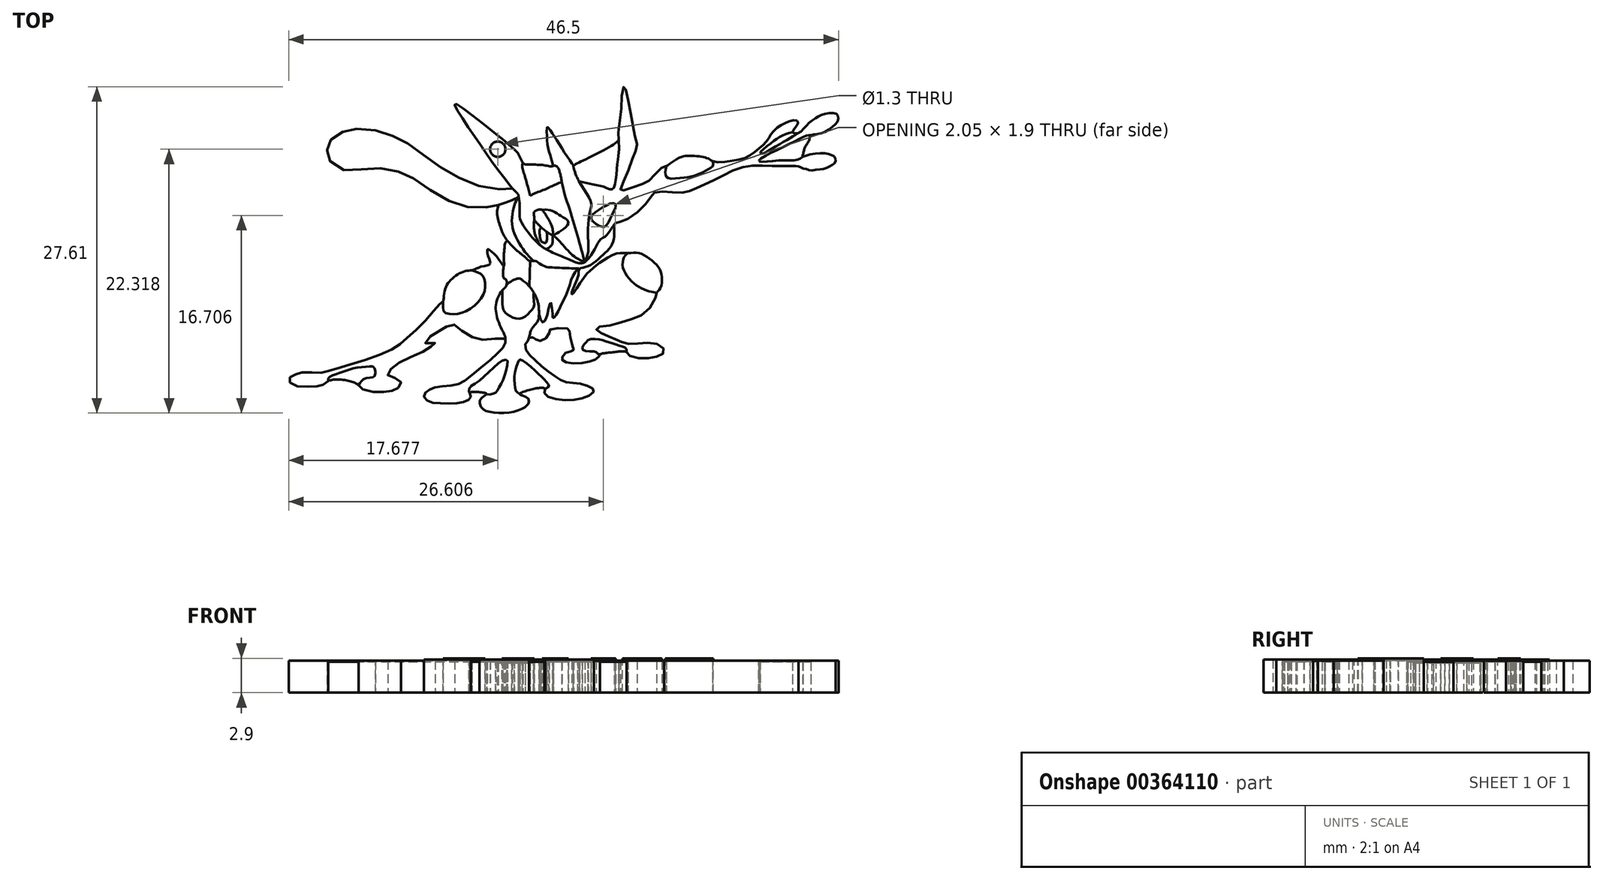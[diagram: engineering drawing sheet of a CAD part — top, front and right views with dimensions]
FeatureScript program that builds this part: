
annotation { "Feature Type Name" : "Feature", "Feature Type Description" : "" }
export const myFeature = defineFeature(function(context is Context, id is Id, definition is map)
    precondition{}
    {
        {
            var Q0;
            Q0=qCreatedBy(makeId("Top.planeOp"),FACE);
            var sketch = newSketch(context, id + "F0", { "sketchPlane" : qUnion([Q0])});
            skFitSpline(sketch, "E0", {"points": [v(20.96, 7.13) * mm, v(21.17, 7.03) * mm, v(21.4, 6.93) * mm, v(21.64, 6.89) * mm, v(21.9, 6.8) * mm, v(22.24, 6.8) * mm, v(22.73, 6.85) * mm, v(23.11, 6.9) * mm, v(23.47, 7.05) * mm, v(23.75, 7.22) * mm, v(23.95, 7.33) * mm, v(24.1, 7.54) * mm, v(24.1, 7.71) * mm, v(24.03, 7.9) * mm, v(23.83, 8.05) * mm, v(23.6, 8.14) * mm, v(23.11, 8.23) * mm, v(22.42, 8.19) * mm, v(21.64, 8.04) * mm, v(21.32, 7.94) * mm, v(21.38, 8.3) * mm, v(21.53, 8.8) * mm, v(21.85, 9.33) * mm, v(22, 9.74) * mm, v(22.47, 9.84) * mm, v(23.3, 10.1) * mm, v(23.97, 10.6) * mm, v(24.32, 11.05) * mm, v(24.27, 11.46) * mm, v(23.96, 11.64) * mm, v(23.1, 11.54) * mm, v(22.55, 11.31) * mm, v(21.95, 10.88) * mm, v(21.44, 10.36) * mm, v(20.9, 9.92) * mm, v(20.44, 10.02) * mm, v(20.63, 10.34) * mm, v(20.9, 10.7) * mm, v(20.9, 10.94) * mm, v(20.66, 11.03) * mm, v(20.12, 10.9) * mm, v(19.6, 10.66) * mm, v(19.05, 10.31) * mm, v(18.63, 9.82) * mm, v(18.36, 9.38) * mm, v(18.02, 8.98) * mm, v(17.3, 8.38) * mm, v(16.47, 7.85) * mm, v(15.29, 7.6) * mm, v(13.88, 7.5) * mm, v(13.36, 7.76) * mm, v(12.7, 7.94) * mm, v(11.76, 8.01) * mm, v(10.8, 7.82) * mm, v(9.8, 7.15) * mm, v(9.6, 7.1) * mm, v(9.06, 6.71) * mm, v(8.45, 6) * mm, v(8.02, 5.76) * mm, v(7.14, 5.4) * mm, v(6.2, 5.1) * mm, v(6.01, 5.05) * mm, v(5.9, 5.17) * mm, v(6.2, 5.92) * mm, v(6.75, 7.35) * mm, v(7.13, 8.3) * mm, v(7.3, 8.8) * mm, v(7.2, 9.4) * mm, v(6.99, 10.4) * mm, v(6.66, 12.13) * mm, v(6.36, 13.55) * mm, v(6.29, 13.84) * mm, v(6.13, 13.8) * mm, v(6, 12.67) * mm, v(5.87, 11.09) * mm, v(5.72, 9.72) * mm, v(5.66, 9.24) * mm, v(2.03, 7.26) * mm, v(1.91, 7.22) * mm, v(1.24, 8.18) * mm, v(0.3, 9.68) * mm, v(-0.21, 10.4) * mm, v(-0.3, 10.44) * mm, v(-0.3, 9.4) * mm, v(-0.1, 8.22) * mm, v(0.15, 7.15) * mm, v(-0.26, 7.17) * mm, v(-1.67, 7.27) * mm, v(-2.36, 7.39) * mm, v(-2.7, 8.13) * mm, v(-3.18, 8.63) * mm, v(-4.36, 9.64) * mm, v(-5.7, 10.68) * mm, v(-7.95, 12.37) * mm, v(-8.14, 12.37) * mm, v(-7.61, 11.39) * mm, v(-6.06, 9.1) * mm, v(-4.7, 7.13) * mm, v(-3.3, 5.33) * mm, v(-3.24, 5.24) * mm, v(-3.8, 5.19) * mm, v(-5.83, 5.38) * mm, v(-8, 6.3) * mm, v(-9.97, 7.48) * mm, v(-11.69, 8.77) * mm, v(-13, 9.52) * mm, v(-14.42, 10.09) * mm, v(-16.33, 10.3) * mm, v(-17.38, 10.13) * mm, v(-18.36, 9.55) * mm, v(-18.81, 9.06) * mm, v(-18.92, 8.39) * mm, v(-18.82, 7.81) * mm, v(-17.88, 6.93) * mm, v(-16.49, 6.8) * mm, v(-14.6, 6.95) * mm, v(-12.94, 6.7) * mm, v(-11.62, 6.1) * mm, v(-9.83, 4.86) * mm, v(-7.8, 3.86) * mm, v(-6.1, 3.63) * mm, v(-4.58, 3.8) * mm, v(-4.43, 3.84) * mm, v(-4.53, 3.33) * mm, v(-4.31, 2.17) * mm, v(-3.93, 1.22) * mm, v(-3.12, 0.24) * mm, v(-2.16, -0.56) * mm], "startDerivative": vector(49.3, -24.54) * mm, "endDerivative": vector(100.47, -77.23) * mm});
            skFitSpline(sketch, "E1", {"points": [v(-3.67, 0.84) * mm, v(-3.85, 0.65) * mm, v(-3.92, 0.1) * mm, v(-3.97, -0.66) * mm, v(-3.97, -1.29) * mm, v(-4.6, -0.48) * mm, v(-5.3, 0.11) * mm, v(-5.35, 0.1) * mm, v(-5.31, -0.46) * mm, v(-5.13, -1.13) * mm, v(-5.89, -1.36) * mm, v(-6.55, -1.64) * mm, v(-7.32, -1.76) * mm, v(-8.32, -2.35) * mm, v(-8.94, -3.3) * mm, v(-9.15, -4.35) * mm, v(-9.35, -4.48) * mm, v(-10.43, -5.76) * mm, v(-12.26, -7.47) * mm, v(-13.42, -8.36) * mm, v(-16.63, -9.53) * mm, v(-18.93, -10.23) * mm, v(-19.51, -10.34) * mm, v(-21.08, -10.32) * mm, v(-21.64, -10.5) * mm, v(-22.15, -10.87) * mm, v(-21.79, -11.37) * mm, v(-20.2, -11.52) * mm, v(-19.39, -11.4) * mm, v(-18.81, -11.03) * mm, v(-17.28, -10.99) * mm, v(-16.28, -11.38) * mm, v(-16.05, -11.67) * mm, v(-14.83, -11.97) * mm, v(-13.72, -11.92) * mm, v(-13.05, -11.72) * mm, v(-12.7, -11.37) * mm, v(-12.8, -10.92) * mm, v(-13.73, -10.63) * mm, v(-13.7, -10.26) * mm, v(-12.9, -9.53) * mm, v(-11, -8.65) * mm, v(-9.97, -8.03) * mm, v(-9.78, -7.83) * mm, v(-10.69, -7.78) * mm, v(-8.46, -6.27) * mm, v(-8.1, -6.32) * mm, v(-6.8, -7.25) * mm, v(-5.38, -7.54) * mm, v(-3.84, -7.45) * mm, v(-3.89, -7.94) * mm, v(-4.56, -8.74) * mm, v(-6.86, -10.7) * mm, v(-8.05, -11.36) * mm, v(-9.67, -11.56) * mm, v(-10.37, -11.84) * mm, v(-10.73, -12.23) * mm, v(-10.47, -12.69) * mm, v(-9.46, -12.92) * mm, v(-7.88, -12.92) * mm, v(-7.04, -12.68) * mm, v(-6.77, -12.39) * mm, v(-6.86, -12.05) * mm, v(-5.87, -12) * mm, v(-5.42, -12.14) * mm, v(-5.95, -12.56) * mm, v(-5.82, -13.33) * mm, v(-5, -13.68) * mm, v(-3.32, -13.68) * mm, v(-2.2, -13.25) * mm, v(-1.9, -12.95) * mm, v(-1.92, -12.51) * mm, v(-2.62, -12.14) * mm, v(-1.7, -11.77) * mm, v(-0.8, -11.61) * mm, v(-0.48, -11.71) * mm, v(-0.53, -12.03) * mm, v(-0.09, -12.44) * mm, v(1.43, -12.65) * mm, v(2.77, -12.46) * mm, v(3.56, -12.04) * mm, v(3.63, -11.78) * mm, v(3.22, -11.5) * mm, v(2.16, -11.22) * mm, v(1.26, -11.14) * mm, v(0.55, -10.75) * mm, v(-0.38, -10.11) * mm, v(-1.5, -9.1) * mm, v(-2.06, -8.45) * mm, v(-2.12, -7.85) * mm, v(-1.9, -7.6) * mm, v(-1.83, -7.35) * mm, v(-1.48, -7.38) * mm, v(-1.26, -7.53) * mm, v(-0.77, -7.64) * mm, v(-0.13, -6.97) * mm, v(-0.1, -6.71) * mm, v(1.46, -6.6) * mm, v(1.6, -6.89) * mm, v(1.84, -8.02) * mm, v(1.9, -8.47) * mm, v(1.36, -8.58) * mm, v(0.98, -9) * mm, v(0.98, -9.26) * mm, v(1.37, -9.48) * mm, v(2.9, -9.48) * mm, v(3.77, -9.2) * mm, v(4.08, -8.97) * mm, v(4.16, -8.8) * mm, v(5.06, -8.63) * mm, v(6.4, -8.59) * mm, v(6.64, -8.87) * mm, v(7.72, -9.12) * mm, v(8.8, -9.03) * mm, v(9.46, -8.75) * mm, v(9.57, -8.36) * mm, v(8.97, -7.9) * mm, v(7.67, -7.85) * mm, v(6.53, -7.9) * mm, v(5.82, -7.68) * mm, v(5.25, -7.43) * mm, v(4.38, -7.02) * mm, v(3.91, -6.74) * mm, v(3.88, -6.53) * mm, v(4.84, -6.36) * mm, v(6.58, -5.86) * mm, v(8.03, -5.24) * mm, v(8.91, -3.83) * mm, v(8.95, -3.57) * mm, v(9.28, -3.16) * mm, v(9.4, -2.31) * mm, v(9.17, -1.5) * mm, v(8.38, -0.7) * mm, v(7.47, -0.21) * mm, v(6.53, -0.22) * mm, v(5.66, -0.23) * mm, v(4.47, -0.8) * mm, v(3.57, -1.48) * mm, v(2.7, -2.42) * mm, v(1.8, -3.7) * mm, v(1.83, -3.4) * mm, v(2.32, -2.14) * mm, v(2.43, -1.55) * mm, v(3.08, -1.36) * mm, v(4.25, -0.53) * mm, v(5.07, 0.33) * mm, v(5.38, 1.34) * mm, v(5.46, 2.32) * mm, v(6.15, 2.5) * mm, v(8.28, 4.22) * mm, v(8.84, 4.93) * mm, v(10.86, 4.9) * mm, v(12.14, 5.2) * mm, v(13.98, 6.04) * mm, v(16.3, 7.08) * mm, v(18.48, 7.16) * mm, v(20.22, 7.16) * mm, v(20.88, 7.15) * mm, v(20.96, 7.13) * mm], "startDerivative": vector(-58.91, -44.68) * mm, "endDerivative": vector(33.26, -8.62) * mm});
            skFitSpline(sketch, "E2", {"points": [v(9.8, 7.15) * mm, v(9.72, 6.86) * mm, v(9.7, 6.43) * mm, v(9.88, 6.14) * mm, v(10.93, 6.13) * mm, v(12, 6.3) * mm, v(12.66, 6.52) * mm, v(13.27, 6.84) * mm, v(13.7, 7.15) * mm, v(13.73, 7.47) * mm, v(13.7, 7.57) * mm], "startDerivative": vector(-1.04, -3.52) * mm, "endDerivative": vector(-0.7, 1.79) * mm});
            skFitSpline(sketch, "E3", {"points": [v(-6.66, -1.66) * mm, v(-6.41, -1.76) * mm, v(-5.85, -2.02) * mm, v(-5.62, -2.47) * mm, v(-5.56, -3.24) * mm, v(-5.84, -4) * mm, v(-6.62, -4.8) * mm, v(-7.6, -5.29) * mm, v(-8.4, -5.38) * mm, v(-9.02, -5.21) * mm, v(-9.12, -4.66) * mm, v(-9.12, -4.3) * mm], "startDerivative": vector(3.66, -1.77) * mm, "endDerivative": vector(-0.23, 4.81) * mm});
            skFitSpline(sketch, "E4", {"points": [v(-18.81, -11.03) * mm, v(-18.78, -10.75) * mm, v(-18.41, -10.55) * mm, v(-17.46, -10.2) * mm, v(-16.37, -9.9) * mm, v(-15.48, -9.83) * mm, v(-14.94, -9.88) * mm, v(-14.89, -10.58) * mm, v(-15.16, -10.75) * mm, v(-15.73, -10.8) * mm, v(-16.07, -11.14) * mm, v(-16.26, -11.4) * mm], "startDerivative": vector(-0.41, 4.83) * mm, "endDerivative": vector(-2.6, -3.68) * mm});
            skFitSpline(sketch, "E5", {"points": [v(-6.86, -12.05) * mm, v(-6.9, -11.9) * mm, v(-6.86, -11.58) * mm, v(-6.25, -11.15) * mm, v(-4.99, -10.03) * mm, v(-4.01, -9.28) * mm, v(-3.68, -9.3) * mm, v(-3.76, -10.1) * mm, v(-4.08, -11.07) * mm, v(-4.43, -11.68) * mm, v(-4.64, -12) * mm, v(-5.08, -12.17) * mm, v(-5.42, -12.14) * mm], "startDerivative": vector(-1.24, 3.18) * mm, "endDerivative": vector(-5.1, 0.94) * mm});
            skFitSpline(sketch, "E6", {"points": [v(-2.62, -12.14) * mm, v(-2.93, -11.9) * mm, v(-3.06, -11.22) * mm, v(-3.01, -10.19) * mm, v(-2.69, -9.28) * mm, v(-2.57, -9.22) * mm, v(-1.62, -9.9) * mm, v(-0.65, -10.82) * mm, v(-0.26, -11.24) * mm, v(-0.15, -11.45) * mm, v(-0.48, -11.71) * mm], "startDerivative": vector(-4.6, 2.26) * mm, "endDerivative": vector(-5.73, -3.11) * mm});
            skFitSpline(sketch, "E7", {"points": [v(4.16, -8.8) * mm, v(3.9, -8.67) * mm, v(3.72, -8.55) * mm, v(2.88, -8.5) * mm, v(2.66, -8.25) * mm, v(2.96, -7.79) * mm, v(3.31, -7.52) * mm, v(4.16, -7.52) * mm, v(4.73, -7.7) * mm, v(5.51, -7.93) * mm, v(5.98, -8.11) * mm, v(6.36, -8.28) * mm, v(6.4, -8.59) * mm], "startDerivative": vector(-4.43, 1.76) * mm, "endDerivative": vector(-0.5, -5.33) * mm});
            skFitSpline(sketch, "E8", {"points": [v(-3.97, -1.29) * mm, v(-3.97, -2.32) * mm, v(-3.76, -2.49) * mm, v(-3.78, -3) * mm, v(-4.1, -3.37) * mm, v(-4.52, -4.1) * mm, v(-4.65, -4.77) * mm, v(-4.58, -5.49) * mm, v(-4.28, -6.37) * mm, v(-3.9, -7.2) * mm, v(-3.84, -7.45) * mm], "startDerivative": vector(-1.31, -10.33) * mm, "endDerivative": vector(0.43, -3.42) * mm});
            skFitSpline(sketch, "E9", {"points": [v(-1.83, -7.35) * mm, v(-1.57, -6.57) * mm, v(-1.1, -5.98) * mm, v(-1, -5.4) * mm, v(-1.07, -4.44) * mm, v(-1.42, -3.6) * mm, v(-1.97, -2.86) * mm, v(-2.45, -2.47) * mm, v(-2.7, -2.36) * mm, v(-3.53, -2.73) * mm, v(-3.78, -3) * mm], "startDerivative": vector(1.59, 7.55) * mm, "endDerivative": vector(-2.18, -3.58) * mm});
            skFitSpline(sketch, "E10", {"points": [v(-4.1, -3.37) * mm, v(-4.1, -4.07) * mm, v(-4.03, -4.98) * mm, v(-3.63, -5.43) * mm, v(-3, -5.75) * mm, v(-2.27, -5.65) * mm, v(-1.67, -5.1) * mm, v(-1.42, -4.7) * mm, v(-1.46, -3.8) * mm, v(-1.42, -3.6) * mm], "startDerivative": vector(0.05, -5.65) * mm, "endDerivative": vector(1.1, 2.3) * mm});
            skFitSpline(sketch, "E11", {"points": [v(6.53, -0.22) * mm, v(6.2, -0.57) * mm, v(6.1, -1.4) * mm, v(6.78, -2.54) * mm, v(7.81, -3.25) * mm, v(8.56, -3.5) * mm, v(8.95, -3.57) * mm], "startDerivative": vector(-2.83, -2.27) * mm, "endDerivative": vector(3.16, -0.34) * mm});
            skFitSpline(sketch, "E12", {"points": [v(-4.43, 3.84) * mm, v(-2.95, 4.4) * mm, v(-2.72, 4.63) * mm, v(-3.24, 5.24) * mm], "startDerivative": vector(3.76, 1.34) * mm, "endDerivative": vector(-2.35, 2.1) * mm});
            skFitSpline(sketch, "E13", {"points": [v(-2.72, 4.63) * mm, v(-2.62, 3.45) * mm, v(-2.59, 2.64) * mm, v(-1.57, 1.11) * mm, v(-0.4, 0.1) * mm, v(1.49, -0.72) * mm, v(2.88, -0.98) * mm, v(4.23, 0.96) * mm, v(4.56, 1.15) * mm, v(5.04, 1.74) * mm, v(5.46, 2.32) * mm], "startDerivative": vector(1.57, -12.87) * mm, "endDerivative": vector(5.28, 7.07) * mm});
            skFitSpline(sketch, "E14", {"points": [v(2.88, -0.98) * mm, v(1.67, -0.23) * mm, v(0.21, 1.24) * mm, v(0.14, 0.61) * mm, v(-0.4, 0.1) * mm], "startDerivative": vector(-3.97, 1.58) * mm, "endDerivative": vector(-3.5, -1.88) * mm});
            skFitSpline(sketch, "E15", {"points": [v(-0.92, 0.46) * mm, v(-1.2, 1.03) * mm, v(-1.4, 1.69) * mm, v(-1.4, 2.6) * mm, v(-1.46, 3.36) * mm, v(-1.72, 4.53) * mm, v(-1.96, 5.44) * mm, v(-2.26, 6.53) * mm, v(-2.42, 7.16) * mm, v(-2.36, 7.39) * mm], "startDerivative": vector(-2.8, 5.5) * mm, "endDerivative": vector(1.35, 3.28) * mm});
            skFitSpline(sketch, "E16", {"points": [v(0.15, 7.15) * mm, v(0.46, 7.15) * mm, v(0.77, 6.59) * mm, v(1.05, 5.26) * mm, v(1.7, 3.15) * mm, v(2.38, 0.79) * mm, v(2.88, -0.98) * mm], "startDerivative": vector(4.06, 0.94) * mm, "endDerivative": vector(2.46, -8.68) * mm});
            skFitSpline(sketch, "E17", {"points": [v(2.88, -0.98) * mm, v(3.16, -0.2) * mm, v(3.16, 1.25) * mm, v(3.3, 3.22) * mm, v(3.4, 4.13) * mm, v(2.28, 6.07) * mm, v(1.91, 7.15) * mm, v(1.91, 7.22) * mm], "startDerivative": vector(2.76, 5.78) * mm, "endDerivative": vector(0.15, 1.41) * mm});
            skFitSpline(sketch, "E18", {"points": [v(0.93, 5.8) * mm, v(0.23, 5.5) * mm, v(-0.55, 5.15) * mm, v(-1.38, 4.82) * mm, v(-1.74, 4.63) * mm], "startDerivative": vector(-2.72, -1.14) * mm, "endDerivative": vector(-1.69, -0.98) * mm});
            skFitSpline(sketch, "E19", {"points": [v(2.4, 5.85) * mm, v(3.52, 5.61) * mm, v(4.68, 5.32) * mm, v(5.27, 5.21) * mm, v(5.6, 7.09) * mm, v(5.77, 8.48) * mm, v(5.74, 9.35) * mm], "startDerivative": vector(6.57, -1.48) * mm, "endDerivative": vector(-0.44, 5.87) * mm});
            skFitSpline(sketch, "E20", {"points": [v(0.21, 1.24) * mm, v(-0.34, 1.59) * mm, v(-1.04, 2.19) * mm, v(-1.4, 2.6) * mm], "startDerivative": vector(-1.65, 0.94) * mm, "endDerivative": vector(-1.1, 1.3) * mm});
            skFitSpline(sketch, "E21", {"points": [v(0.21, 1.24) * mm, v(0.09, 2.06) * mm, v(-0.25, 2.74) * mm, v(-0.59, 3.27) * mm, v(-0.81, 3.47) * mm, v(-1.26, 3.37) * mm, v(-1.44, 3.21) * mm], "startDerivative": vector(-0.3, 3.98) * mm, "endDerivative": vector(-1.25, -1.48) * mm});
            skFitSpline(sketch, "E22", {"points": [v(-0.72, 3.42) * mm, v(-0.3, 3.45) * mm, v(0.3, 3.27) * mm, v(0.87, 2.92) * mm, v(1.4, 2.55) * mm, v(1.46, 2.22) * mm, v(0.89, 1.68) * mm, v(0.4, 1.4) * mm, v(0.21, 1.24) * mm], "startDerivative": vector(3.5, 0.5) * mm, "endDerivative": vector(-2.02, -1.76) * mm});
            skFitSpline(sketch, "E23", {"points": [v(-2.16, -0.56) * mm, v(-1.76, -0.89) * mm, v(-1.35, -0.88) * mm, v(-0.64, -1.29) * mm, v(0.21, -1.44) * mm, v(1.63, -1.5) * mm, v(2.28, -1.52) * mm, v(2.43, -1.55) * mm], "startDerivative": vector(3.03, -3.41) * mm, "endDerivative": vector(1.85, -0.45) * mm});
            skFitSpline(sketch, "E24", {"points": [v(-1.76, -0.89) * mm, v(-1.8, -3.03) * mm], "startDerivative": vector(-0.05, -2.15) * mm, "endDerivative": vector(-0.05, -2.15) * mm});
            skFitSpline(sketch, "E25", {"points": [v(2.28, -1.52) * mm, v(1.82, -2.25) * mm, v(1.52, -3.2) * mm, v(0.82, -4.73) * mm, v(0.43, -5.48) * mm, v(0.21, -5.71) * mm, v(0.15, -5.37) * mm, v(0, -4.4) * mm, v(-0.27, -5.3) * mm, v(-0.51, -5.95) * mm, v(-0.69, -6.07) * mm, v(-1, -5.4) * mm], "startDerivative": vector(-5.26, -7.15) * mm, "endDerivative": vector(-3.3, 10.27) * mm});
            skFitSpline(sketch, "E26", {"points": [v(4.56, 2) * mm, v(4.95, 2.5) * mm, v(5.24, 3.13) * mm, v(5.46, 3.58) * mm, v(5.46, 3.93) * mm, v(5.2, 4.01) * mm, v(4.25, 3.56) * mm, v(3.52, 3) * mm, v(3.45, 2.6) * mm, v(4.13, 2.08) * mm, v(4.56, 2) * mm]});
            skFitSpline(sketch, "E27", {"points": [v(-1.46, -0.87) * mm, v(-2.16, -0.14) * mm, v(-2.85, 0.96) * mm, v(-3.26, 2.14) * mm, v(-3.2, 3.27) * mm, v(-2.99, 4.08) * mm, v(-2.76, 4.53) * mm], "startDerivative": vector(-4.17, 4.05) * mm, "endDerivative": vector(2, 3.5) * mm});
            skFitSpline(sketch, "E28", {"points": [v(21.32, 7.94) * mm, v(20.82, 7.66) * mm, v(19.39, 7.63) * mm, v(17.79, 7.5) * mm, v(17.6, 7.6) * mm, v(18.63, 8.25) * mm, v(20.88, 9.37) * mm, v(21.74, 9.75) * mm, v(22, 9.74) * mm], "startDerivative": vector(-4.49, -3.53) * mm, "endDerivative": vector(3.55, -0.56) * mm});
            skFitSpline(sketch, "E29", {"points": [v(20.9, 9.92) * mm, v(20.22, 9.5) * mm, v(18.98, 8.77) * mm, v(17.88, 8.21) * mm, v(17.73, 8.29) * mm, v(18.6, 9.05) * mm, v(19.47, 9.67) * mm, v(20.44, 10.02) * mm], "startDerivative": vector(-4.72, -3.05) * mm, "endDerivative": vector(6.8, 1.99) * mm});
            skCircle(sketch, "E30", {"center": v(-4.48, 8.57) * mm, "radius": 0.65 * mm});
            skFitSpline(sketch, "E31", {"points": [v(-0.8, 1.97) * mm, v(-0.95, 1.7) * mm, v(-0.9, 1.1) * mm, v(-0.78, 0.76) * mm, v(-0.58, 0.67) * mm, v(-0.4, 0.68) * mm, v(-0.32, 1.34) * mm, v(-0.34, 1.59) * mm], "startDerivative": vector(-1.4, -1.77) * mm, "endDerivative": vector(-0.17, 1.55) * mm});
            skFitSpline(sketch, "E32", {"points": [v(-0.48, 1.69) * mm, v(-0.5, 1.34) * mm, v(-0.6, 1.23) * mm, v(-0.72, 1.41) * mm, v(-0.75, 1.72) * mm, v(-0.71, 1.89) * mm], "startDerivative": vector(0.1, -1.55) * mm, "endDerivative": vector(0.28, 0.88) * mm});
            skSolve(sketch);
        }
        {
            var Q0;
            {var subQ4=sQuery(id+"F0.wireOp",EDGE,"E7");Q0=makeQuery(id+"F0.imprint","IMPRINT",FACE,{"disambiguationData":[TD([[makeQuery(id+"F0.imprint","IMPRINT",EDGE,{"derivedFrom":subQ4}),1.0]])]});}
            var Q1;
            {var subQ0=sQuery(id+"F0.wireOp",EDGE,"E3");Q1=makeQuery(id+"F0.imprint","IMPRINT",FACE,{"disambiguationData":[TD([[makeQuery(id+"F0.imprint","IMPRINT",EDGE,{"derivedFrom":subQ0}),1.0]])]});}
            var Q2;
            {var subQ9=sQuery(id+"F0.wireOp",EDGE,"E2");Q2=makeQuery(id+"F0.imprint","IMPRINT",FACE,{"disambiguationData":[TD([[makeQuery(id+"F0.imprint","IMPRINT",EDGE,{"derivedFrom":subQ9}),-1.0]])]});}
            var Q3;
            {var subQ3=sQuery(id+"F0.wireOp",EDGE,"E18");Q3=makeQuery(id+"F0.imprint","IMPRINT",FACE,{"disambiguationData":[TD([[makeQuery(id+"F0.imprint","IMPRINT",EDGE,{"derivedFrom":subQ3}),1.0]])]});}
            var Q4;
            Q4=makeQuery(id+"F0.imprint","IMPRINT",FACE,{"disambiguationData":[TD([[makeQuery(id+"F0.imprint","IMPRINT",EDGE,{"derivedFrom":sQuery(id+"F0.wireOp",EDGE,"E30")}),-1.0]])]});
            extrude(context, id + "F1", {"entities" : qUnion([Q0, Q1, Q2, Q3, Q4]), "depth" : 2.7 * mm});
        }
        {
            var Q0;
            {var subQ0=sQuery(id+"F0.wireOp",EDGE,"E3");Q0=makeQuery(id+"F0.imprint","IMPRINT",FACE,{"disambiguationData":[TD([[makeQuery(id+"F0.imprint","IMPRINT",EDGE,{"derivedFrom":subQ0}),-1.0]])]});}
            var Q1;
            {var subQ3=sQuery(id+"F0.wireOp",EDGE,"E10");Q1=makeQuery(id+"F0.imprint","IMPRINT",FACE,{"disambiguationData":[TD([[makeQuery(id+"F0.imprint","IMPRINT",EDGE,{"derivedFrom":subQ3}),1.0]])]});}
            var Q2;
            {var subQ0=sQuery(id+"F0.wireOp",EDGE,"E11");Q2=makeQuery(id+"F0.imprint","IMPRINT",FACE,{"disambiguationData":[TD([[makeQuery(id+"F0.imprint","IMPRINT",EDGE,{"derivedFrom":subQ0}),1.0]])]});}
            var Q3;
            {var subQ0=sQuery(id+"F0.wireOp",EDGE,"E22");Q3=makeQuery(id+"F0.imprint","IMPRINT",FACE,{"disambiguationData":[TD([[makeQuery(id+"F0.imprint","IMPRINT",EDGE,{"derivedFrom":subQ0}),-1.0]])]});}
            var Q4;
            Q4=makeQuery(id+"F0.imprint","IMPRINT",FACE,{"disambiguationData":[TD([[makeQuery(id+"F0.imprint","IMPRINT",EDGE,{"derivedFrom":sQuery(id+"F0.wireOp",EDGE,"E26")}),1.0]])]});
            var Q5;
            {var subQ0=sQuery(id+"F0.wireOp",EDGE,"E2");Q5=makeQuery(id+"F0.imprint","IMPRINT",FACE,{"disambiguationData":[TD([[makeQuery(id+"F0.imprint","IMPRINT",EDGE,{"derivedFrom":subQ0}),1.0]])]});}
            extrude(context, id + "F2", {"entities" : qUnion([Q0, Q1, Q2, Q3, Q4, Q5]), "depth" : 2.9 * mm});
        }
        {
            var Q0;
            {var subQ0=sQuery(id+"F0.wireOp",EDGE,"E4");Q0=makeQuery(id+"F0.imprint","IMPRINT",FACE,{"disambiguationData":[TD([[makeQuery(id+"F0.imprint","IMPRINT",EDGE,{"derivedFrom":subQ0}),-1.0]])]});}
            var Q1;
            {var subQ0=sQuery(id+"F0.wireOp",EDGE,"E5");Q1=makeQuery(id+"F0.imprint","IMPRINT",FACE,{"disambiguationData":[TD([[makeQuery(id+"F0.imprint","IMPRINT",EDGE,{"derivedFrom":subQ0}),-1.0]])]});}
            var Q2;
            {var subQ0=sQuery(id+"F0.wireOp",EDGE,"E6");Q2=makeQuery(id+"F0.imprint","IMPRINT",FACE,{"disambiguationData":[TD([[makeQuery(id+"F0.imprint","IMPRINT",EDGE,{"derivedFrom":subQ0}),-1.0]])]});}
            var Q3;
            {var subQ0=sQuery(id+"F0.wireOp",EDGE,"E7");Q3=makeQuery(id+"F0.imprint","IMPRINT",FACE,{"disambiguationData":[TD([[makeQuery(id+"F0.imprint","IMPRINT",EDGE,{"derivedFrom":subQ0}),-1.0]])]});}
            var Q4;
            {var subQ0=sQuery(id+"F0.wireOp",EDGE,"E28");Q4=makeQuery(id+"F0.imprint","IMPRINT",FACE,{"disambiguationData":[TD([[makeQuery(id+"F0.imprint","IMPRINT",EDGE,{"derivedFrom":subQ0}),-1.0]])]});}
            var Q5;
            {var subQ0=sQuery(id+"F0.wireOp",EDGE,"E29");Q5=makeQuery(id+"F0.imprint","IMPRINT",FACE,{"disambiguationData":[TD([[makeQuery(id+"F0.imprint","IMPRINT",EDGE,{"derivedFrom":subQ0}),-1.0]])]});}
            extrude(context, id + "F3", {"entities" : qUnion([Q0, Q1, Q2, Q3, Q4, Q5]), "depth" : 2.6 * mm});
        }
        {
            var Q0;
            {var subQ4=sQuery(id+"F0.wireOp",EDGE,"E5");Q0=makeQuery(id+"F0.imprint","IMPRINT",FACE,{"disambiguationData":[TD([[makeQuery(id+"F0.imprint","IMPRINT",EDGE,{"derivedFrom":subQ4}),1.0]])]});}
            var Q1;
            {var subQ3=sQuery(id+"F0.wireOp",EDGE,"E24");Q1=makeQuery(id+"F0.imprint","IMPRINT",FACE,{"disambiguationData":[TD([[makeQuery(id+"F0.imprint","IMPRINT",EDGE,{"derivedFrom":subQ3}),-1.0]])]});}
            extrude(context, id + "F4", {"entities" : qUnion([Q0, Q1]), "depth" : 2.8 * mm});
        }
        {
            var Q0;
            {var subQ5=sQuery(id+"F0.wireOp",EDGE,"E24");Q0=makeQuery(id+"F0.imprint","IMPRINT",FACE,{"disambiguationData":[TD([[makeQuery(id+"F0.imprint","IMPRINT",EDGE,{"derivedFrom":subQ5}),1.0]])]});}
            extrude(context, id + "F5", {"entities" : qUnion([Q0]), "depth" : 2.8 * mm});
        }
        {
            var Q0;
            {var subQ1=sQuery(id+"F0.wireOp",EDGE,"E16");var subQ4=sQuery(id+"F0.wireOp",EDGE,"E0");var subQ5=makeQuery(id+"F0.imprint","INTERSECT",VERTEX,{"derivedFrom":[subQ4,subQ1]});Q0=makeQuery(id+"F0.imprint","IMPRINT",FACE,{"disambiguationData":[TD([[makeQuery(id+"F0.imprint","IMPRINT",EDGE,{"disambiguationData":[TD([[subQ5,1.0]])],"derivedFrom":subQ4}),1.0]])]});}
            extrude(context, id + "F6", {"entities" : qUnion([Q0]), "depth" : 2.8 * mm});
        }
        {
            var Q0;
            {var subQ3=sQuery(id+"F0.wireOp",EDGE,"E19");Q0=makeQuery(id+"F0.imprint","IMPRINT",FACE,{"disambiguationData":[TD([[makeQuery(id+"F0.imprint","IMPRINT",EDGE,{"derivedFrom":subQ3}),1.0]])]});}
            var Q1;
            {var subQ5=sQuery(id+"F0.wireOp",EDGE,"E18");Q1=makeQuery(id+"F0.imprint","IMPRINT",FACE,{"disambiguationData":[TD([[makeQuery(id+"F0.imprint","IMPRINT",EDGE,{"derivedFrom":subQ5}),-1.0]])]});}
            extrude(context, id + "F7", {"entities" : qUnion([Q0, Q1]), "depth" : 2.6 * mm});
        }
        {
            var Q0;
            Q0=makeQuery(id+"F0.imprint","IMPRINT",FACE,{"disambiguationData":[TD([[makeQuery(id+"F0.imprint","IMPRINT",EDGE,{"derivedFrom":sQuery(id+"F0.wireOp",EDGE,"E30")}),1.0]])]});
            var Q1;
            Q1=sQuery(id+"F0.wireOp",EDGE,"E30");
            extrude(context, id + "F8", {"entities" : qUnion([Q0]), "operationType" : NewBodyOperationType.REMOVE, "surfaceEntities" : qUnion([Q1]), "oppositeDirection" : true, "depth" : 3 * mm});
        }
        {
            var Q0;
            {var subQ0=sQuery(id+"F0.wireOp",EDGE,"E12");var subQ1=sQuery(id+"F0.wireOp",EDGE,"E0");var subQ2=makeQuery(id+"F0.imprint","INTERSECT",VERTEX,{"disambiguationData":[OD(0.0)],"derivedFrom":[subQ1,subQ0]});Q0=makeQuery(id+"F0.imprint","IMPRINT",FACE,{"disambiguationData":[TD([[makeQuery(id+"F0.imprint","IMPRINT",EDGE,{"disambiguationData":[TD([[subQ2,1.0]])],"derivedFrom":subQ1}),1.0]])]});}
            extrude(context, id + "F9", {"entities" : qUnion([Q0]), "operationType" : NewBodyOperationType.ADD, "depth" : 2.6 * mm});
        }
        {
            var Q0;
            {var subQ7=sQuery(id+"F0.wireOp",EDGE,"E27");Q0=makeQuery(id+"F0.imprint","IMPRINT",FACE,{"disambiguationData":[TD([[makeQuery(id+"F0.imprint","IMPRINT",EDGE,{"derivedFrom":subQ7}),1.0]])]});}
            extrude(context, id + "F10", {"entities" : qUnion([Q0]), "depth" : 2.5 * mm});
        }
        {
            var Q0;
            {var subQ6=sQuery(id+"F0.wireOp",EDGE,"E27");Q0=makeQuery(id+"F0.imprint","IMPRINT",FACE,{"disambiguationData":[TD([[makeQuery(id+"F0.imprint","IMPRINT",EDGE,{"derivedFrom":subQ6}),-1.0]])]});}
            extrude(context, id + "F11", {"entities" : qUnion([Q0]), "depth" : 2.6 * mm});
        }
        {
            var Q0;
            {var subQ1=sQuery(id+"F0.wireOp",EDGE,"E20");var subQ4=sQuery(id+"F0.wireOp",EDGE,"E15");var subQ5=makeQuery(id+"F0.imprint","INTERSECT",VERTEX,{"derivedFrom":[subQ4,subQ1]});Q0=makeQuery(id+"F0.imprint","IMPRINT",FACE,{"disambiguationData":[TD([[makeQuery(id+"F0.imprint","IMPRINT",EDGE,{"disambiguationData":[TD([[subQ5,-1.0]])],"derivedFrom":subQ4}),-1.0]])]});}
            extrude(context, id + "F12", {"entities" : qUnion([Q0]), "depth" : 2.7 * mm});
        }
        {
            var Q0;
            {var subQ3=sQuery(id+"F0.wireOp",EDGE,"E31");Q0=makeQuery(id+"F0.imprint","IMPRINT",FACE,{"disambiguationData":[TD([[makeQuery(id+"F0.imprint","IMPRINT",EDGE,{"derivedFrom":subQ3}),-1.0]])]});}
            extrude(context, id + "F13", {"entities" : qUnion([Q0]), "depth" : 2.6 * mm});
        }
        {
            var Q0;
            {var subQ0=sQuery(id+"F0.wireOp",EDGE,"E31");Q0=makeQuery(id+"F0.imprint","IMPRINT",FACE,{"disambiguationData":[TD([[makeQuery(id+"F0.imprint","IMPRINT",EDGE,{"derivedFrom":subQ0}),1.0]])]});}
            var Q1;
            {var subQ0=sQuery(id+"F0.wireOp",EDGE,"E32");Q1=makeQuery(id+"F0.imprint","IMPRINT",FACE,{"disambiguationData":[TD([[makeQuery(id+"F0.imprint","IMPRINT",EDGE,{"derivedFrom":subQ0}),-1.0]])]});}
            extrude(context, id + "F14", {"entities" : qUnion([Q0, Q1]), "depth" : 2.5 * mm});
        }
        {
            var Q0;
            {var subQ0=sQuery(id+"F0.wireOp",EDGE,"E14");var subQ1=sQuery(id+"F0.wireOp",EDGE,"E13");var subQ3=makeQuery(id+"F0.imprint","INTERSECT",VERTEX,{"derivedFrom":[subQ1,subQ0]});Q0=makeQuery(id+"F0.imprint","IMPRINT",FACE,{"disambiguationData":[TD([[makeQuery(id+"F0.imprint","IMPRINT",EDGE,{"disambiguationData":[TD([[subQ3,-1.0]])],"derivedFrom":subQ1}),1.0]])]});}
            extrude(context, id + "F15", {"entities" : qUnion([Q0]), "depth" : 2.7 * mm});
        }
    });
